# Revit family: Haworth_Cultivate_Table
name_source: partatom
category: Furniture Systems
revit_build: Autodesk Revit 2018 (Build: 20170223_1515(x64)
units: mm (PartAtom-declared; Revit-internal decimal feet)

## family parameters
Always vertical = Yes
Cut with Voids When Loaded = No
OmniClass Number = 23.40.70.14.64.21
OmniClass Title = Systems Furniture
Part Type = Normal
Room Calculation Point = No
Round Connector Dimension = Use Diameter
Shared = No
Work Plane-Based = No

## types (10) — shared parameters
Actual Height = 42"
Assembly Code = E2020200
Bag Hook = No
Bag Hook Finish = Haworth _ Paint _ Metallic Champagne
Base Only = No
Custom Size = No
Description = Haworth - Cultivate Table
Footrest x1 = No
Footrest x2 = Yes
Frame Height = 40"
Frame Height 28 in. = No
Frame Height 40 in. = Yes
Manufacturer = Haworth
Max. Depth = 42"
Max. Width = 134"
Min. Depth = 36"
Min. Width = 60"
Min/Max Width = 60-120 in.; or 79-115 in.; or 98-134 in. @ 12 in. increments
Model = Haworth - Cultivate Table
Revision Number = 1
Size = Verify Final Dim. w/ Haworth
Standard Depths = 36, 42 in.
Standard Height = 29, 30, 41, 41 in.
Standard Top Thickness = 1 3/16, 2 in.
Support Finish = Haworth _ Paint _ Metallic Champagne
Support Height = 40"
Sustainability Info = https://www.haworth.com
Top Included = Yes
Top Thickness = 2"
Top Thickness 1 3/16 in. = No
Top Thickness 2 in. = Yes
URL = www.haworth.com
URL - Product = http://www.haworth.com
Vertical Wire Manager = No
Warranty = http://www.haworth.com
Wire Manager Height = 37 53/64"
Worksurface Edge Finish = Haworth _ Laminate _ Maple H-AE
Worksurface Finish = Haworth _ Laminate _ Maple H-AE

## per-type parameters (varying)
| type | Actual Depth | Actual Top Overhang - Both Sides - 19 in. | Actual Top Overhang - Both Sides - 24 in. | Actual Top Overhang - Left Side | Actual Top Overhang - Right Side | Actual Top Overhang - Right Side - 19 in. | Actual Top Overhang - Right Side - 24 in. | Actual Width | Depth | Table Seam | Top Overhang - Both Sides - 19 in. | Top Overhang - Both Sides - 24 in. | Top Overhang - None | Top Overhang - Right Side - 19 in. | Top Overhang - Right Side - 24 in. | Width |
| 42h 60w 36d - Top Overhang - None | 36" | 0" | 0" | 0" | 0" | 0" | 0" | 60" | 36" | No | No | No | Yes | No | No | 60" |
| 42h 120w 42d - Top Overhang - None | 42" | 0" | 0" | 0" | 0" | 0" | 0" | 120" | 42" | No | No | No | Yes | No | No | 120" |
| 42h 103w 42d - Top Overhang - Right | 42" | 0" | 0" | 0" | 19" | 19" | 0" | 103" | 42" | No | No | No | No | Yes | No | 103" |
| 42h 108w 42d - Top Overhang - Both Sides | 42" | 0" | 24" | 24" | 24" | 0" | 0" | 108" | 42" | No | No | Yes | No | No | No | 108" |
| 42h 122w 42d - Top Overhang - Both Sides | 42" | 19" | 0" | 19" | 19" | 0" | 0" | 122" | 42" | Yes | Yes | No | No | No | No | 122" |
| 42h 79w 36d - Top Overhang - Right | 36" | 0" | 0" | 0" | 19" | 19" | 0" | 79" | 36" | No | No | No | No | Yes | No | 79" |
| 42h 72w 36d - Top Overhang - None | 36" | 0" | 0" | 0" | 0" | 0" | 0" | 72" | 36" | No | No | No | Yes | No | No | 72" |
| 42h 84w 36d - Top Overhang - Right | 36" | 0" | 0" | 0" | 24" | 0" | 24" | 84" | 36" | No | No | No | No | No | Yes | 84" |
| 42h 84w 36d - Top Overhang - None | 36" | 0" | 0" | 0" | 0" | 0" | 0" | 84" | 36" | No | No | No | Yes | No | No | 84" |
| 42h 96w 42d | 42" | 0" | 0" | 0" | 0" | 0" | 0" | 96" | 42" | No | No | No | Yes | No | No | 96" |

## geometry (parser evidence)
native form markers: Sweep x6
no freeform markers — native parametric forms only
